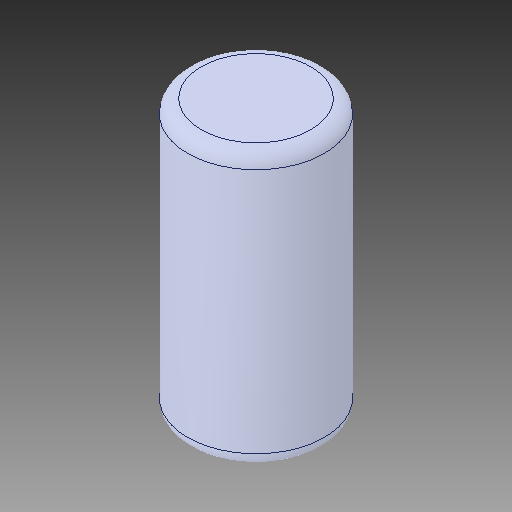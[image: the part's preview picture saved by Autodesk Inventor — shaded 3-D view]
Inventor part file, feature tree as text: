
AUTODESK INVENTOR PART (.ipt)
format: ipt  version: 2019 (Build 230136000, 136)  size: 117,248 bytes
history: native  units: in
note: dims shown in document units (in); Inventor stores cm internally (conversion verified against a paired STEP export)
features: fillet x1
ambient origin geometry x8: Origin, YZ Plane, XZ Plane, XY Plane, X Axis, Y Axis, Z Axis, Center Point
bodies: Solid1 (feature_tree)
feature tree (1):
  fillet  "Fillet1"  [1 undecoded]
note: 1 required parameter value undecoded (feature->parameter linkage not recoverable at this tier; creation-order binding heuristic only, values carry confidence <= 0.55)
